# Revit family: Haworth_BuzziPicNic_WorkBenchCollaborativeTable
name_source: partatom
category: Furniture
revit_build: Autodesk Revit 2018 (Build: 20170223_1515(x64)
units: mm (PartAtom-declared; Revit-internal decimal feet)

## family parameters
Always vertical = Yes
Cut with Voids When Loaded = No
OmniClass Number = 23.40.20.00
OmniClass Title = General Furniture and Specialties
Room Calculation Point = No
Shared = No
Work Plane-Based = No

## types (2) — shared parameters
Assembly Code = E2020200
Base Finish = Haworth _ Wood _ Natural Ash BAS-NAT
Glide Finish = Haworth _ Polymer _ Black
Manufacturer = Haworth
Model = HCBZ-PNTW
Revision = 1
Size = Verify Final Dim. w/ Haworth
URL = http://www.haworth.com
URL - Product = https://www.haworth.com
Warranty = http://www.haworth.com
zero-valued in all types: Actual Depth, Actual Height, Actual Width

## per-type parameters (varying)
| type | Description | Laminate Top | Wood Top |
| HCBZ-PNTW-W | Haworth BuzziPicNic WorkBench Collaborative Table - Wood Top | No | Yes |
| HCBZ-PNTW-L | Haworth BuzziPicNic WorkBench Collaborative Table - Laminate Top | Yes | No |

## geometry (parser evidence)
native form markers: Sweep x4
no freeform markers — native parametric forms only
